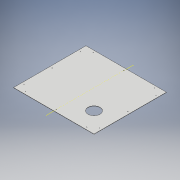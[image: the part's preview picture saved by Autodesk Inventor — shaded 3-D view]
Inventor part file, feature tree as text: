
AUTODESK INVENTOR PART (.ipt)
format: ipt  version: 2018 (Build 220112000, 112)  size: 135,168 bytes
history: native  units: mm
features: other x1, extrude x1, sketch x1
ambient origin geometry x8: Origin, YZ Plane, XZ Plane, XY Plane, X Axis, Y Axis, Z Axis, Center Point
bodies: Body1 (feature_tree)
feature tree (3):
  other  "Bryła1"
  extrude  "Wyciągnięcie proste1"  Depth=1000.0mm
  sketch  "Szkic1"
